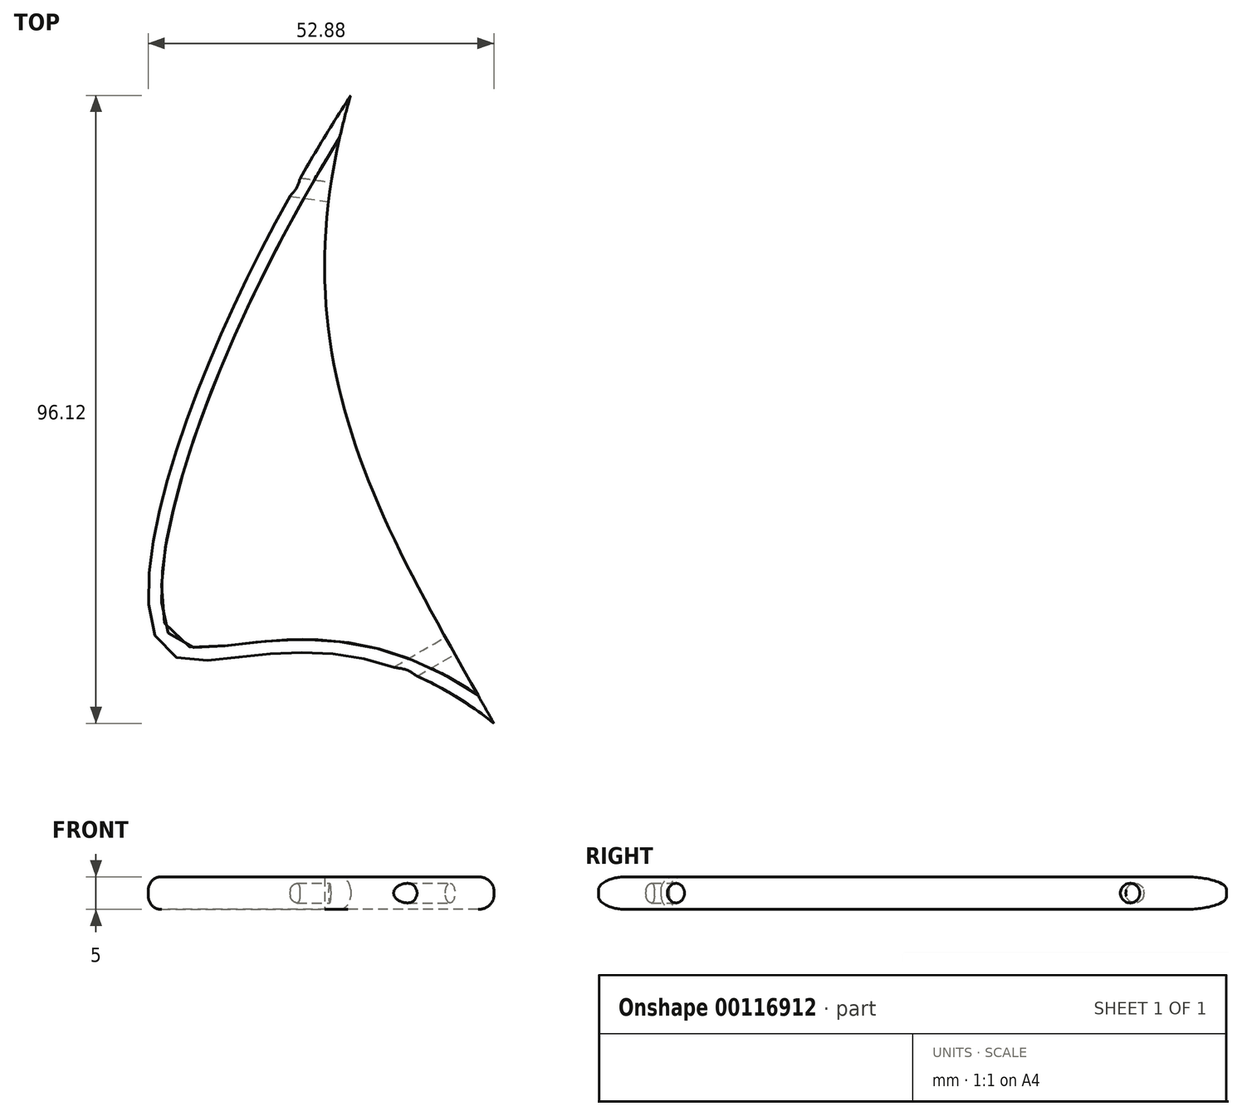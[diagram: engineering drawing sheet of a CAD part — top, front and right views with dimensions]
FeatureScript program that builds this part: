
annotation { "Feature Type Name" : "Feature", "Feature Type Description" : "" }
export const myFeature = defineFeature(function(context is Context, id is Id, definition is map)
    precondition{}
    {
        {
            var Q0;
            Q0=qCreatedBy(makeId("Top.planeOp"),FACE);
            var sketch = newSketch(context, id + "F0", { "sketchPlane" : qUnion([Q0])});
            skLineSegment(sketch, "E0", {"start": v(4.1, -58.98) * mm, "end": v(4.1, 41.02) * mm});
            skLineSegment(sketch, "E1", {"start": v(-44.4, -54.98) * mm, "end": v(-39.4, -54.98) * mm});
            skFitSpline(sketch, "E2", {"points": [v(-39.4, -54.98) * mm, v(-65.9, 66.02) * mm], "startDerivative": vector(-65.27, 124.48) * mm, "endDerivative": vector(60.74, 155.97) * mm});
            skLineSegment(sketch, "E3", {"start": v(-69.83, 6.02) * mm, "end": v(4.1, 6.02) * mm});
            skLineSegment(sketch, "E4", {"start": v(4.1, -58.98) * mm, "end": v(-45.4, -58.98) * mm});
            skLineSegment(sketch, "E5", {"start": v(-45.4, -58.98) * mm, "end": v(-55.06, -41.74) * mm});
            skLineSegment(sketch, "E6", {"start": v(-55.06, -41.74) * mm, "end": v(-58.48, -38.79) * mm});
            skLineSegment(sketch, "E7", {"start": v(-58.48, -38.79) * mm, "end": v(-58.48, -58.98) * mm});
            skLineSegment(sketch, "E8", {"start": v(-58.48, -58.98) * mm, "end": v(-45.4, -58.98) * mm});
            skLineSegment(sketch, "E9", {"start": v(66.68, -38.79) * mm, "end": v(66.68, -58.98) * mm});
            skLineSegment(sketch, "E10.MirrorCS", {"start": v(63.26, -41.74) * mm, "end": v(66.68, -38.79) * mm});
            skLineSegment(sketch, "E11.MirrorCS", {"start": v(66.68, -58.98) * mm, "end": v(53.6, -58.98) * mm});
            skLineSegment(sketch, "E12.MirrorCS", {"start": v(4.1, -58.98) * mm, "end": v(53.6, -58.98) * mm});
            skLineSegment(sketch, "E13.MirrorCS", {"start": v(53.6, -58.98) * mm, "end": v(63.26, -41.74) * mm});
            skPoint(sketch, "E14.0.internal.snap0", {"position": v(-56.77, -40.26) * mm});
            skFitSpline(sketch, "E14", {"points": [v(-47.47, -40.26) * mm, v(-97.41, -29.43) * mm, v(-69.38, 55.86) * mm], "startDerivative": vector(-170.86, 135.96) * mm, "endDerivative": vector(131.14, 202.22) * mm});
            skLineSegment(sketch, "E15", {"start": v(-39.4, -54.98) * mm, "end": v(-34.4, -54.98) * mm});
            skLineSegment(sketch, "E16", {"start": v(-34.4, -54.98) * mm, "end": v(-34.4, -16.98) * mm});
            skLineSegment(sketch, "E17", {"start": v(-51.28, -26.73) * mm, "end": v(-34.4, -16.98) * mm});
            skLineSegment(sketch, "E18", {"start": v(-57.65, -15.7) * mm, "end": v(-45.16, -37.34) * mm});
            skLineSegment(sketch, "E19", {"start": v(-29.4, -54.98) * mm, "end": v(-29.4, 35.02) * mm});
            skLineSegment(sketch, "E20", {"start": v(-29.4, 35.02) * mm, "end": v(-66.86, 40.28) * mm});
            skLineSegment(sketch, "E21", {"start": v(-68.6, 27.92) * mm, "end": v(-65.2, 52.07) * mm});
            skSolve(sketch);
        }
        {
            var Q0;
            {var subQ2=sQuery(id+"F0.wireOp",EDGE,"E14");Q0=makeQuery(id+"F0.imprint","IMPRINT",FACE,{"disambiguationData":[TD([[makeQuery(id+"F0.imprint","IMPRINT",EDGE,{"derivedFrom":subQ2}),-1.0]])]});}
            extrude(context, id + "F1", {"entities" : qUnion([Q0]), "endBound" : BoundingType.SYMMETRIC, "depth" : 5 * mm});
        }
        {
            var Q0;
            Q0=qCreatedBy(makeId("Front.planeOp"),FACE);
            var Q1;
            Q1=sQuery(id+"F0.wireOp",EDGE,"E18");
            cPlane(context, id + "F2", {"entities" : qUnion([Q0, Q1]), "cplaneType" : CPlaneType.LINE_ANGLE, "offset" : 150 * mm, "angle" : 0 * degree, "width" : 150 * mm, "height" : 150 * mm});
        }
        {
            var Q0;
            Q0=qCreatedBy(id+"F2.planeOp",FACE);
            var sketch = newSketch(context, id + "F3", { "sketchPlane" : qUnion([Q0])});
            skPoint(sketch, "E22", {"position": v(2.5, 0) * mm});
            skSolve(sketch);
        }
        {
            var Q0;
            Q0=sQuery(id+"F3.wireOp",VERTEX,"E22");
            var Q1;
            Q1=makeQuery(id+"F1.opExtrude","SWEPT_BODY",BODY,{"disambiguationData":[OSD([sQuery(id+"F0.wireOp",EDGE,"E2"),sQuery(id+"F0.wireOp",EDGE,"E14")])]});
            hole(context, id + "F4", {"style" : HoleStyle.SIMPLE, "holeDiameter" : 3 * mm, "endStyle" : HoleEndStyle.THROUGH, "locations" : qUnion([Q0]), "scope" : qUnion([Q1])});
        }
        {
            var Q0;
            Q0=qCreatedBy(makeId("Front.planeOp"),FACE);
            var Q1;
            Q1=sQuery(id+"F0.wireOp",EDGE,"E21");
            cPlane(context, id + "F5", {"entities" : qUnion([Q0, Q1]), "cplaneType" : CPlaneType.LINE_ANGLE, "offset" : 150 * mm, "angle" : 0 * degree, "width" : 150 * mm, "height" : 150 * mm});
        }
        {
            var Q0;
            Q0=qCreatedBy(id+"F5.planeOp",FACE);
            var sketch = newSketch(context, id + "F6", { "sketchPlane" : qUnion([Q0])});
            skPoint(sketch, "E23", {"position": v(-30.58, 0) * mm});
            skSolve(sketch);
        }
        {
            var Q0;
            Q0=sQuery(id+"F6.wireOp",VERTEX,"E23");
            var Q1;
            Q1=makeQuery(id+"F1.opExtrude","SWEPT_BODY",BODY,{"disambiguationData":[OSD([sQuery(id+"F0.wireOp",EDGE,"E2"),sQuery(id+"F0.wireOp",EDGE,"E14")])]});
            hole(context, id + "F7", {"style" : HoleStyle.SIMPLE, "holeDiameter" : 3 * mm, "endStyle" : HoleEndStyle.THROUGH, "oppositeDirection" : true, "locations" : qUnion([Q0]), "scope" : qUnion([Q1])});
        }
        {
            var Q0;
            Q0=makeQuery(id+"F1.opExtrude","CAP_EDGE",EDGE,{"disambiguationData":[OSD([sQuery(id+"F0.wireOp",EDGE,"E14")])],"isStart":false});
            var Q1;
            Q1=makeQuery(id+"F1.opExtrude","CAP_EDGE",EDGE,{"disambiguationData":[OSD([sQuery(id+"F0.wireOp",EDGE,"E14")])],"isStart":true});
            fillet(context, id + "F8", {"entities" : qUnion([Q0, Q1]), "radius" : 2 * mm, "tangentPropagation" : true, "allowEdgeOverflow" : false});
        }
    });
